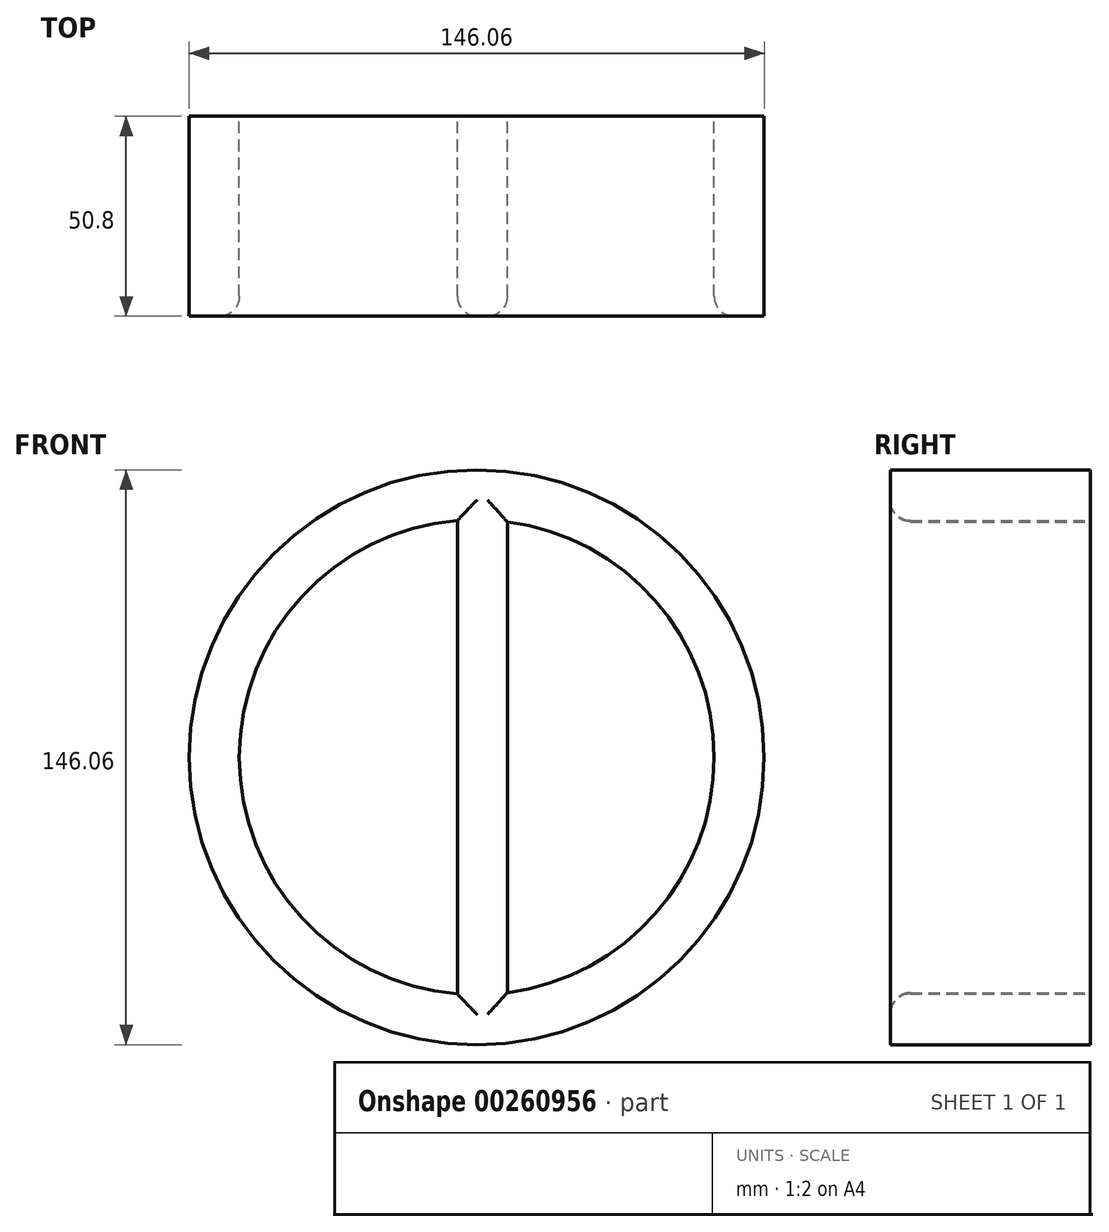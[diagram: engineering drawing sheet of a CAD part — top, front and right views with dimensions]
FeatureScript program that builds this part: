
annotation { "Feature Type Name" : "Feature", "Feature Type Description" : "" }
export const myFeature = defineFeature(function(context is Context, id is Id, definition is map)
    precondition{}
    {
        {
            var Q0;
            Q0=qCreatedBy(makeId("Front.planeOp"),FACE);
            var sketch = newSketch(context, id + "F0", { "sketchPlane" : qUnion([Q0])});
            skCircle(sketch, "E0", {"center": v(0, 0) * mm, "radius": 73.03 * mm});
            skLineSegment(sketch, "E1", {"start": v(7.76, 72.61) * mm, "end": v(7.76, -72.61) * mm});
            skLineSegment(sketch, "E2", {"start": v(7.76, -72.61) * mm, "end": v(-4.94, -72.86) * mm});
            skLineSegment(sketch, "E3", {"start": v(-4.94, -72.86) * mm, "end": v(-4.94, 72.86) * mm});
            skCircle(sketch, "E4", {"center": v(0, 0) * mm, "radius": 60.33 * mm});
            skPoint(sketch, "E5", {"position": v(0, 52.7) * mm});
            skSolve(sketch);
        }
        {
            var Q0;
            {var subQ0=sQuery(id+"F0.wireOp",EDGE,"E2");Q0=makeQuery(id+"F0.imprint","IMPRINT",FACE,{"disambiguationData":[TD([[makeQuery(id+"F0.imprint","IMPRINT",EDGE,{"derivedFrom":subQ0}),1.0]])]});}
            var Q1;
            {var subQ0=sQuery(id+"F0.wireOp",EDGE,"E3");var subQ1=sQuery(id+"F0.wireOp",EDGE,"E0");var subQ3=makeQuery(id+"F0.imprint","INTERSECT",VERTEX,{"derivedFrom":[subQ1,subQ0]});Q1=makeQuery(id+"F0.imprint","IMPRINT",FACE,{"disambiguationData":[TD([[makeQuery(id+"F0.imprint","IMPRINT",EDGE,{"disambiguationData":[TD([[subQ3,1.0]])],"derivedFrom":subQ0}),1.0]])]});}
            var Q2;
            {var subQ0=sQuery(id+"F0.wireOp",EDGE,"E1");var subQ1=sQuery(id+"F0.wireOp",EDGE,"E0");var subQ2=makeQuery(id+"F0.imprint","INTERSECT",VERTEX,{"derivedFrom":[subQ1,subQ0]});Q2=makeQuery(id+"F0.imprint","IMPRINT",FACE,{"disambiguationData":[TD([[makeQuery(id+"F0.imprint","IMPRINT",EDGE,{"disambiguationData":[TD([[subQ2,-1.0]])],"derivedFrom":subQ0}),1.0]])]});}
            var Q3;
            {var subQ0=sQuery(id+"F0.wireOp",EDGE,"E2");Q3=makeQuery(id+"F0.imprint","IMPRINT",FACE,{"disambiguationData":[TD([[makeQuery(id+"F0.imprint","IMPRINT",EDGE,{"derivedFrom":subQ0}),-1.0]])]});}
            var Q4;
            {var subQ0=sQuery(id+"F0.wireOp",EDGE,"E4");var subQ1=sQuery(id+"F0.wireOp",EDGE,"E1");var subQ2=makeQuery(id+"F0.imprint","INTERSECT",VERTEX,{"disambiguationData":[OD(0.0)],"derivedFrom":[subQ1,subQ0]});Q4=makeQuery(id+"F0.imprint","IMPRINT",FACE,{"disambiguationData":[TD([[makeQuery(id+"F0.imprint","IMPRINT",EDGE,{"disambiguationData":[TD([[subQ2,-1.0]])],"derivedFrom":subQ1}),-1.0]])]});}
            var Q5;
            {var subQ0=sQuery(id+"F0.wireOp",EDGE,"E1");var subQ1=sQuery(id+"F0.wireOp",EDGE,"E0");var subQ2=makeQuery(id+"F0.imprint","INTERSECT",VERTEX,{"derivedFrom":[subQ1,subQ0]});Q5=makeQuery(id+"F0.imprint","IMPRINT",FACE,{"disambiguationData":[TD([[makeQuery(id+"F0.imprint","IMPRINT",EDGE,{"disambiguationData":[TD([[subQ2,-1.0]])],"derivedFrom":subQ1}),1.0]])]});}
            extrude(context, id + "F1", {"entities" : qUnion([Q0, Q1, Q2, Q3, Q4, Q5]), "depth" : 50.8 * mm});
        }
        {
            var Q0;
            {var subQ0=sQuery(id+"F0.wireOp",EDGE,"E4");var subQ1=sQuery(id+"F0.wireOp",EDGE,"E3");Q0=makeQuery(id+"F1.opExtrude","CAP_EDGE",EDGE,{"disambiguationData":[OSD([subQ0]),TDD([makeQuery(id+"F0.imprint","IMPRINT",EDGE,{"disambiguationData":[TD([[makeQuery(id+"F0.imprint","INTERSECT",VERTEX,{"disambiguationData":[OD(0.0)],"derivedFrom":[subQ1,subQ0]}),1.0]])],"derivedFrom":subQ0})])],"isStart":false});}
            var Q1;
            {var subQ0=sQuery(id+"F0.wireOp",EDGE,"E4");var subQ1=sQuery(id+"F0.wireOp",EDGE,"E1");Q1=makeQuery(id+"F1.opExtrude","CAP_EDGE",EDGE,{"disambiguationData":[OSD([subQ0]),TDD([makeQuery(id+"F0.imprint","IMPRINT",EDGE,{"disambiguationData":[TD([[makeQuery(id+"F0.imprint","INTERSECT",VERTEX,{"disambiguationData":[OD(0.0)],"derivedFrom":[subQ1,subQ0]}),1.0]])],"derivedFrom":subQ0})])],"isStart":false});}
            var Q2;
            Q2=makeQuery(id+"F1.opExtrude","CAP_EDGE",EDGE,{"disambiguationData":[OSD([sQuery(id+"F0.wireOp",EDGE,"E3")])],"isStart":false});
            var Q3;
            Q3=makeQuery(id+"F1.opExtrude","CAP_EDGE",EDGE,{"disambiguationData":[OSD([sQuery(id+"F0.wireOp",EDGE,"E1")])],"isStart":false});
            fillet(context, id + "F2", {"entities" : qUnion([Q0, Q1, Q2, Q3]), "radius" : 5.08 * mm, "tangentPropagation" : true, "allowEdgeOverflow" : false});
        }
    });
